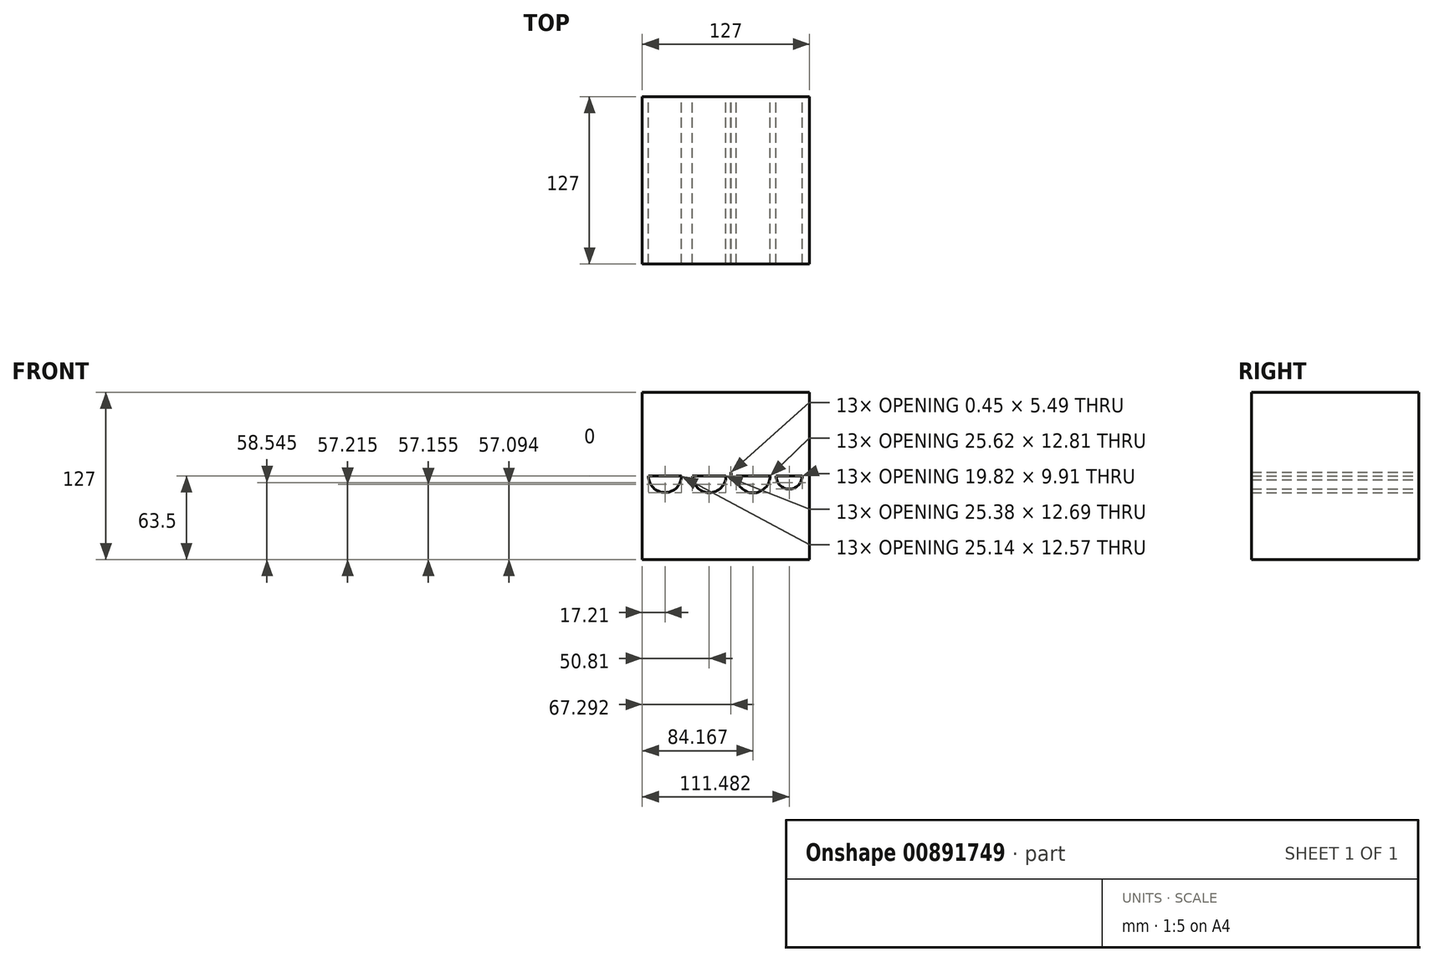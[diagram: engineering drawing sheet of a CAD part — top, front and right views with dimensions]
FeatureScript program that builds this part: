
annotation { "Feature Type Name" : "Feature", "Feature Type Description" : "" }
export const myFeature = defineFeature(function(context is Context, id is Id, definition is map)
    precondition{}
    {
        {
            var Q0;
            Q0=qCreatedBy(makeId("Front.planeOp"),FACE);
            var sketch = newSketch(context, id + "F0", { "sketchPlane" : qUnion([Q0])});
            skLineSegment(sketch, "E0.bottom", {"start": v(63.5, 63.5) * mm, "end": v(-63.5, 63.5) * mm});
            skLineSegment(sketch, "E0.top", {"start": v(63.5, -63.5) * mm, "end": v(-63.5, -63.5) * mm});
            skLineSegment(sketch, "E0.left", {"start": v(63.5, 63.5) * mm, "end": v(63.5, -63.5) * mm});
            skLineSegment(sketch, "E0.right", {"start": v(-63.5, 63.5) * mm, "end": v(-63.5, -63.5) * mm});
            skPoint(sketch, "E0.middle", {"position": v(0, 0) * mm});
            skLineSegment(sketch, "E1", {"start": v(-63.5, 0) * mm, "end": v(63.5, 0) * mm});
            skArc(sketch, "E2", {"start": v(-58.86, 0) * mm, "mid": v(-46.29, -12.57) * mm, "end": v(-33.72, 0) * mm});
            skLineSegment(sketch, "E3", {"start": v(-58.86, 0) * mm, "end": v(-33.72, 0) * mm});
            skArc(sketch, "E4", {"start": v(-25.38, 0) * mm, "mid": v(-12.7, -12.7) * mm, "end": v(0, 0) * mm});
            skArc(sketch, "E5", {"start": v(7.86, 0) * mm, "mid": v(20.67, -12.81) * mm, "end": v(33.48, 0) * mm});
            skArc(sketch, "E6", {"start": v(38.07, 0) * mm, "mid": v(47.98, -9.91) * mm, "end": v(57.9, 0) * mm});
            skCircle(sketch, "E7", {"center": v(-46.29, 0) * mm, "radius": 16.44 * mm});
            skCircle(sketch, "E8", {"center": v(-12.7, 0) * mm, "radius": 16.7 * mm});
            skCircle(sketch, "E9", {"center": v(20.67, 0) * mm, "radius": 17.1 * mm});
            skCircle(sketch, "E10", {"center": v(47.98, 0) * mm, "radius": 12.06 * mm});
            skLineSegment(sketch, "E11.bottom", {"start": v(63.5, 20.43) * mm, "end": v(-63.5, 20.43) * mm});
            skLineSegment(sketch, "E11.top", {"start": v(63.5, -20.43) * mm, "end": v(-63.5, -20.43) * mm});
            skLineSegment(sketch, "E11.left", {"start": v(63.5, 20.43) * mm, "end": v(63.5, -20.43) * mm});
            skLineSegment(sketch, "E11.right", {"start": v(-63.5, 20.43) * mm, "end": v(-63.5, -20.43) * mm});
            skSolve(sketch);
        }
        {
            var Q0;
            {var subQ0=sQuery(id+"F0.wireOp",EDGE,"E0.bottom");Q0=makeQuery(id+"F0.imprint","IMPRINT",FACE,{"disambiguationData":[TD([[makeQuery(id+"F0.imprint","IMPRINT",EDGE,{"derivedFrom":subQ0}),1.0]])]});}
            var Q1;
            {var subQ0=sQuery(id+"F0.wireOp",EDGE,"E0.top");Q1=makeQuery(id+"F0.imprint","IMPRINT",FACE,{"disambiguationData":[TD([[makeQuery(id+"F0.imprint","IMPRINT",EDGE,{"derivedFrom":subQ0}),-1.0]])]});}
            var Q2;
            {var subQ9=sQuery(id+"F0.wireOp",EDGE,"E11.top");Q2=makeQuery(id+"F0.imprint","IMPRINT",FACE,{"disambiguationData":[TD([[makeQuery(id+"F0.imprint","IMPRINT",EDGE,{"derivedFrom":subQ9}),-1.0]])]});}
            var Q3;
            {var subQ5=sQuery(id+"F0.wireOp",EDGE,"E11.bottom");Q3=makeQuery(id+"F0.imprint","IMPRINT",FACE,{"disambiguationData":[TD([[makeQuery(id+"F0.imprint","IMPRINT",EDGE,{"derivedFrom":subQ5}),1.0]])]});}
            var Q4;
            {var subQ5=sQuery(id+"F0.wireOp",EDGE,"E4");Q4=makeQuery(id+"F0.imprint","IMPRINT",FACE,{"disambiguationData":[TD([[makeQuery(id+"F0.imprint","IMPRINT",EDGE,{"derivedFrom":subQ5}),-1.0]])]});}
            var Q5;
            {var subQ1=sQuery(id+"F0.wireOp",EDGE,"E1");var subQ5=sQuery(id+"F0.wireOp",EDGE,"E4");var subQ8=makeQuery(id+"F0.imprint","INTERSECT",VERTEX,{"disambiguationData":[OD(0.0)],"derivedFrom":[subQ1,subQ5]});Q5=makeQuery(id+"F0.imprint","IMPRINT",FACE,{"disambiguationData":[TD([[makeQuery(id+"F0.imprint","IMPRINT",EDGE,{"disambiguationData":[TD([[subQ8,-1.0]])],"derivedFrom":subQ1}),1.0]])]});}
            var Q6;
            {var subQ0=sQuery(id+"F0.wireOp",EDGE,"E2");var subQ1=sQuery(id+"F0.wireOp",EDGE,"E1");var subQ2=makeQuery(id+"F0.imprint","INTERSECT",VERTEX,{"disambiguationData":[OD(0.0)],"derivedFrom":[subQ1,subQ0]});Q6=makeQuery(id+"F0.imprint","IMPRINT",FACE,{"disambiguationData":[TD([[makeQuery(id+"F0.imprint","IMPRINT",EDGE,{"disambiguationData":[TD([[subQ2,-1.0]])],"derivedFrom":subQ1}),1.0]])]});}
            var Q7;
            {var subQ1=sQuery(id+"F0.wireOp",EDGE,"E1");var subQ5=sQuery(id+"F0.wireOp",EDGE,"E5");var subQ6=makeQuery(id+"F0.imprint","INTERSECT",VERTEX,{"disambiguationData":[OD(0.0)],"derivedFrom":[subQ1,subQ5]});Q7=makeQuery(id+"F0.imprint","IMPRINT",FACE,{"disambiguationData":[TD([[makeQuery(id+"F0.imprint","IMPRINT",EDGE,{"disambiguationData":[TD([[subQ6,-1.0]])],"derivedFrom":subQ1}),1.0]])]});}
            var Q8;
            {var subQ0=sQuery(id+"F0.wireOp",EDGE,"E6");var subQ1=sQuery(id+"F0.wireOp",EDGE,"E1");var subQ2=makeQuery(id+"F0.imprint","INTERSECT",VERTEX,{"disambiguationData":[OD(0.0)],"derivedFrom":[subQ1,subQ0]});Q8=makeQuery(id+"F0.imprint","IMPRINT",FACE,{"disambiguationData":[TD([[makeQuery(id+"F0.imprint","IMPRINT",EDGE,{"disambiguationData":[TD([[subQ2,-1.0]])],"derivedFrom":subQ1}),1.0]])]});}
            var Q9;
            {var subQ5=sQuery(id+"F0.wireOp",EDGE,"E6");Q9=makeQuery(id+"F0.imprint","IMPRINT",FACE,{"disambiguationData":[TD([[makeQuery(id+"F0.imprint","IMPRINT",EDGE,{"derivedFrom":subQ5}),-1.0]])]});}
            var Q10;
            {var subQ0=sQuery(id+"F0.wireOp",EDGE,"E10");var subQ1=sQuery(id+"F0.wireOp",EDGE,"E1");var subQ2=makeQuery(id+"F0.imprint","INTERSECT",VERTEX,{"disambiguationData":[OD(1.0)],"derivedFrom":[subQ1,subQ0]});Q10=makeQuery(id+"F0.imprint","IMPRINT",FACE,{"disambiguationData":[TD([[makeQuery(id+"F0.imprint","IMPRINT",EDGE,{"disambiguationData":[TD([[subQ2,-1.0]])],"derivedFrom":subQ1}),-1.0]])]});}
            var Q11;
            {var subQ0=sQuery(id+"F0.wireOp",EDGE,"E10");var subQ1=sQuery(id+"F0.wireOp",EDGE,"E1");var subQ2=makeQuery(id+"F0.imprint","INTERSECT",VERTEX,{"disambiguationData":[OD(1.0)],"derivedFrom":[subQ1,subQ0]});Q11=makeQuery(id+"F0.imprint","IMPRINT",FACE,{"disambiguationData":[TD([[makeQuery(id+"F0.imprint","IMPRINT",EDGE,{"disambiguationData":[TD([[subQ2,-1.0]])],"derivedFrom":subQ1}),1.0]])]});}
            var Q12;
            {var subQ5=sQuery(id+"F0.wireOp",EDGE,"E5");Q12=makeQuery(id+"F0.imprint","IMPRINT",FACE,{"disambiguationData":[TD([[makeQuery(id+"F0.imprint","IMPRINT",EDGE,{"derivedFrom":subQ5}),-1.0]])]});}
            var Q13;
            {var subQ0=sQuery(id+"F0.wireOp",EDGE,"E2");Q13=makeQuery(id+"F0.imprint","IMPRINT",FACE,{"disambiguationData":[TD([[makeQuery(id+"F0.imprint","IMPRINT",EDGE,{"derivedFrom":subQ0}),-1.0]])]});}
            extrude(context, id + "F1", {"entities" : qUnion([Q0, Q1, Q2, Q3, Q4, Q5, Q6, Q7, Q8, Q9, Q10, Q11, Q12, Q13]), "depth" : 127 * mm, "offsetDistance" : 25.4 * mm});
        }
    });
